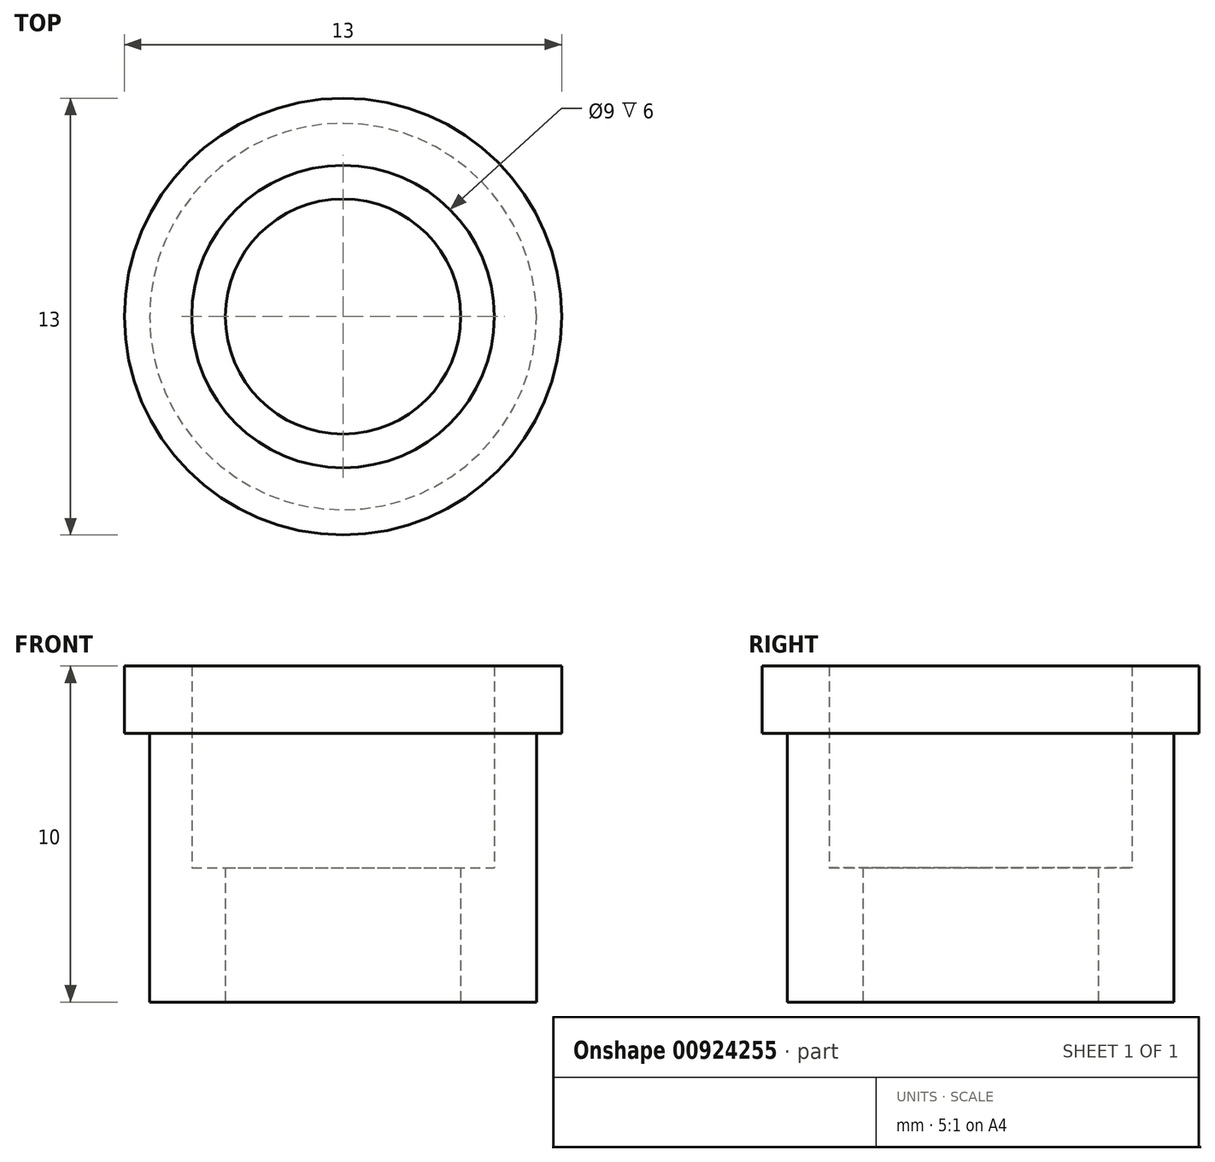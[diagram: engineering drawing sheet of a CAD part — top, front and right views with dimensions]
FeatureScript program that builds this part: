
annotation { "Feature Type Name" : "Feature", "Feature Type Description" : "" }
export const myFeature = defineFeature(function(context is Context, id is Id, definition is map)
    precondition{}
    {
        {
            var Q0;
            Q0=qCreatedBy(makeId("Front.planeOp"),FACE);
            var sketch = newSketch(context, id + "F0", { "sketchPlane" : qUnion([Q0])});
            skLineSegment(sketch, "E0", {"start": v(0, 0) * mm, "end": v(0, 20.52) * mm, "construction": true});
            skLineSegment(sketch, "E1", {"start": v(0, 0) * mm, "end": v(3.5, 0) * mm, "construction": true});
            skLineSegment(sketch, "E2", {"start": v(3.5, 0) * mm, "end": v(3.5, 4) * mm});
            skLineSegment(sketch, "E3", {"start": v(3.5, 4) * mm, "end": v(4.5, 4) * mm});
            skLineSegment(sketch, "E4", {"start": v(4.5, 4) * mm, "end": v(4.5, 10) * mm});
            skLineSegment(sketch, "E5", {"start": v(4.5, 10) * mm, "end": v(6.5, 10) * mm});
            skLineSegment(sketch, "E6", {"start": v(6.5, 10) * mm, "end": v(6.5, 8) * mm});
            skLineSegment(sketch, "E7", {"start": v(6.5, 8) * mm, "end": v(5.75, 8) * mm});
            skLineSegment(sketch, "E8", {"start": v(5.75, 8) * mm, "end": v(5.75, 0) * mm});
            skLineSegment(sketch, "E9", {"start": v(5.75, 0) * mm, "end": v(3.5, 0) * mm});
            skSolve(sketch);
        }
        {
            var Q0;
            Q0 = qSketchRegion(id + "F0", true);
            var Q1;
            Q1=sQuery(id+"F0.wireOp",EDGE,"E0");
            revolve(context, id + "F1", {"surfaceOperationType" : NewSurfaceOperationType.NEW, "entities" : qUnion([Q0]), "axis" : qUnion([Q1]), "revolveType" : RevolveType.FULL});
        }
    });
